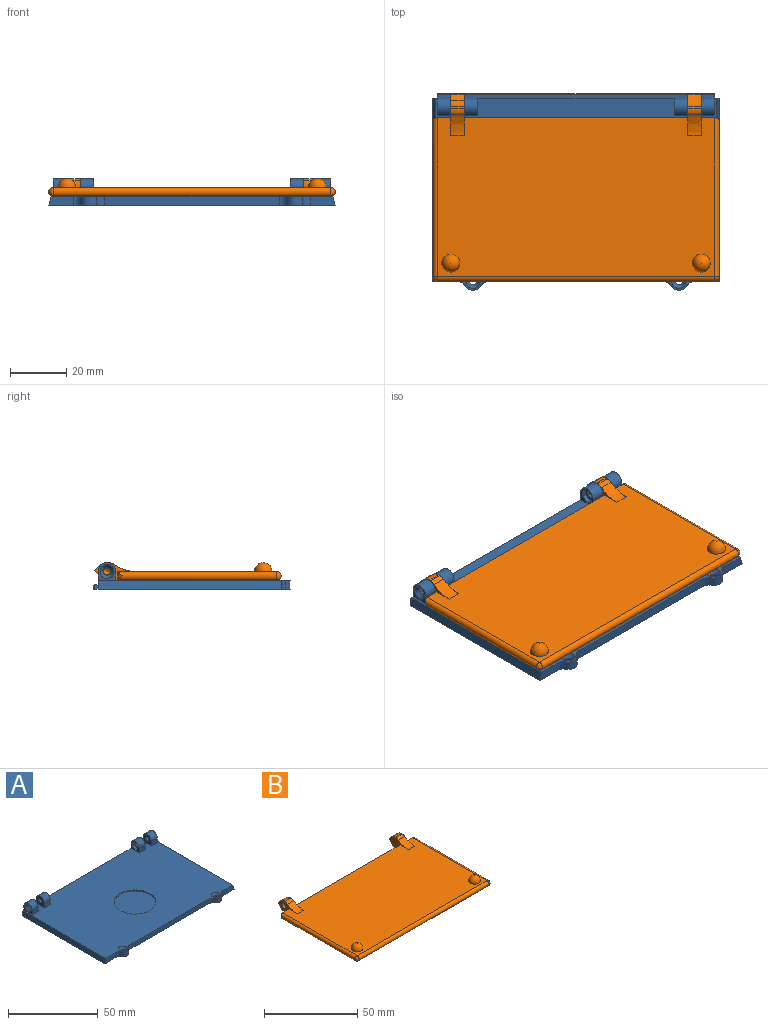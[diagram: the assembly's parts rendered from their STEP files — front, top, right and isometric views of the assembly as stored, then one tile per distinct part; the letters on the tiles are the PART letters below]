
ASSEMBLY  parts=2 mates=1
PART A: 66 faces, bbox 101.9x70.2x10.1 mm
  f0: plane 6.35x6.35mm, normal (-1,0,0), area 16.2mm2, adj f2,f9,f37,f39,f49,f50,f51,f52
  f1: plane 6.35x6.35mm, normal (1,0,0), area 16.2mm2, adj f2,f9,f32,f40,f42,f43,f44,f45
  f2: plane 100.27x68.62mm, normal (0,0,1), area 5950.8mm2, adj f0,f1,f3,f4,f8,f9,f12,f13
  f3: plane 8.77x3.18mm, normal (0,-1,0), area 26.6mm2, adj f2,f7,f15,f27,f65
  f4: plane 62x3.18mm, normal (0,-1,0), area 196.9mm2, adj f2,f7,f14,f16
  f5: plane 97.94x1.09mm, normal (0,1,0), area 107mm2, adj f22,f23,f24,f25
  f6: plane 98.45x1.32mm, normal (0,0,1), area 130mm2, adj f9,f10,f11,f24
  f7: plane 101.46x69.94mm, normal (0,0,-1), area 6733.1mm2, adj f3,f4,f8,f9,f10,f11,f12,f13
  f8: plane 8.77x3.18mm, normal (0,-1,0), area 26.6mm2, adj f2,f7,f17,f26,f64
  f9: plane 101.53x6.35mm, normal (0,1,0), area 222.8mm2, adj f0,f1,f2,f6,f7,f10,f11,f26
  f10: plane 1.6x1.32mm, normal (1,0,0), area 2.1mm2, adj f6,f7,f9,f25
  f11: plane 1.6x1.32mm, normal (-1,0,0), area 2.1mm2, adj f6,f7,f9,f22
  f12: cylinder r=3.17mm len=5.5mm, axis (0,0,1), area 21.1mm2, adj f2,f7,f14,f15
  f13: cylinder r=3.17mm len=5.5mm, axis (0,0,-1), area 21.1mm2, adj f2,f7,f16,f17
  f14: bspline ~3.49x2.75mm, area 10.6mm2, adj f2,f4,f7,f12
  f15: bspline ~3.49x2.75mm, area 10.6mm2, adj f2,f3,f7,f12
  f16: bspline ~3.49x2.75mm, area 10.6mm2, adj f2,f4,f7,f13
  f17: bspline ~3.49x2.75mm, area 10.6mm2, adj f2,f7,f8,f13
  f18: cylinder r=1.27mm len=2.54mm, axis (0,0,1), area 14.2mm2, adj f7,f20
  f19: cylinder r=1.27mm len=2.54mm, axis (0,0,1), area 14.2mm2, adj f7,f21
  f20: cone r=1.27mm half-angle=41deg, axis (0,0,1), area 21.8mm2, adj f2,f18
  f21: cone r=1.27mm half-angle=41deg, axis (0,0,1), area 21.8mm2, adj f2,f19
  f22: cylinder r=0.25mm len=1.6mm, axis (0,0,-1), area 0.5mm2, adj f5,f11,f23,f24
  f23: cylinder r=0.25mm len=98.45mm, axis (1,0,0), area 39.2mm2, adj f5,f7,f22,f25
  f24: cylinder r=0.25mm len=98.45mm, axis (-1,0,0), area 39.2mm2, adj f5,f6,f22,f25
  f25: cylinder r=0.25mm len=1.6mm, axis (0,0,1), area 0.5mm2, adj f5,f10,f23,f24
  f26: cylinder r=0.25mm len=65.08mm, axis (0,1,0), area 17.3mm2, adj f7,f8,f9,f64
  f27: cylinder r=0.25mm len=65.08mm, axis (0,-1,0), area 17.3mm2, adj f3,f7,f9,f65
  f28: plane 6.35x6.35mm, normal (-1,0,0), area 16.6mm2, adj f2,f9,f29,f41,f61
  f29: plane 4.76x3.18mm, normal (0,-1,0), area 15.1mm2, adj f2,f28,f30,f41
  f30: plane 6.35x6.35mm, normal (1,0,0), area 30.9mm2, adj f2,f9,f29,f41,f59
  f31: plane 6.35x6.35mm, normal (-1,0,0), area 30.9mm2, adj f2,f9,f32,f40,f57
  f32: plane 4.76x3.18mm, normal (0,-1,0), area 15.1mm2, adj f1,f2,f31,f40
  f33: plane 6.35x6.35mm, normal (1,0,0), area 16.6mm2, adj f2,f9,f35,f38,f60
  f34: plane 6.35x6.35mm, normal (-1,0,0), area 30.9mm2, adj f2,f9,f35,f38,f58
  f35: plane 4.76x3.18mm, normal (0,-1,0), area 15.1mm2, adj f2,f33,f34,f38
  f36: plane 6.35x6.35mm, normal (1,0,0), area 30.9mm2, adj f2,f9,f37,f39,f56
  f37: plane 4.76x3.18mm, normal (0,-1,0), area 15.1mm2, adj f0,f2,f36,f39
  f38: cylinder r=3.17mm len=6.35mm, axis (-1,0,0), area 47.5mm2, adj f9,f33,f34,f35
  f39: cylinder r=3.17mm len=6.35mm, axis (-1,0,0), area 47.5mm2, adj f0,f9,f36,f37
  f40: cylinder r=3.17mm len=6.35mm, axis (-1,0,0), area 47.5mm2, adj f1,f9,f31,f32
  f41: cylinder r=3.17mm len=6.35mm, axis (-1,0,0), area 47.5mm2, adj f9,f28,f29,f30
  f42: plane 2.39x1.6mm, normal (0,0.5,-0.87), area 4.4mm2, adj f1,f43,f47,f48
  f43: plane 2.76x1.6mm, normal (0,1,0), area 4.4mm2, adj f1,f42,f44,f48
  f44: plane 2.39x1.6mm, normal (0,0.5,0.87), area 4.4mm2, adj f1,f43,f45,f48
  f45: plane 2.39x1.6mm, normal (0,-0.5,0.87), area 4.4mm2, adj f1,f44,f46,f48
  f46: plane 2.76x1.6mm, normal (0,-1,0), area 4.4mm2, adj f1,f45,f47,f48
  f47: plane 2.39x1.6mm, normal (0,-0.5,-0.87), area 4.4mm2, adj f1,f42,f46,f48
  f48: plane 5.51x4.78mm, normal (1,0,0), area 14.7mm2, adj f42,f43,f44,f45,f46,f47,f57
  f49: plane 2.39x1.59mm, normal (0,-0.5,-0.87), area 4.4mm2, adj f0,f50,f54,f55
  f50: plane 2.76x1.59mm, normal (0,-1,0), area 4.4mm2, adj f0,f49,f51,f55
  f51: plane 2.39x1.59mm, normal (0,-0.5,0.87), area 4.4mm2, adj f0,f50,f52,f55
  f52: plane 2.39x1.59mm, normal (0,0.5,0.87), area 4.4mm2, adj f0,f51,f53,f55
  f53: plane 2.76x1.59mm, normal (0,1,0), area 4.4mm2, adj f0,f52,f54,f55
  f54: plane 2.39x1.59mm, normal (0,0.5,-0.87), area 4.4mm2, adj f0,f49,f53,f55
  f55: plane 5.51x4.78mm, normal (-1,0,0), area 14.7mm2, adj f49,f50,f51,f52,f53,f54,f56
  f56: cylinder r=1.27mm len=3.18mm, axis (-1,0,0), area 25.3mm2, adj f36,f55
  f57: cylinder r=1.27mm len=3.16mm, axis (1,0,0), area 25.2mm2, adj f31,f48
  f58: cylinder r=1.27mm len=3.37mm, axis (1,0,0), area 26.9mm2, adj f34,f60
  f59: cylinder r=1.27mm len=3.37mm, axis (-1,0,0), area 26.9mm2, adj f30,f61
  f60: cone r=1.27mm half-angle=41deg, axis (1,0,0), area 21.8mm2, adj f33,f58
  f61: cone r=1.27mm half-angle=41deg, axis (-1,0,0), area 21.8mm2, adj f28,f59
  f62: cylinder r=11.63mm len=23.26mm, axis (0,0,1), area 57.9mm2, adj f2,f63
  f63: plane 23.26x23.26mm, normal (0,0,1), area 425mm2, adj f62
  f64: plane 65.08x3.05mm, normal (-0.97,0,0.26), area 205.3mm2, adj f2,f8,f9,f26
  f65: plane 65.08x3.05mm, normal (0.97,0,0.26), area 205.3mm2, adj f2,f3,f9,f27
PART B: 36 faces, bbox 102.7x67.3x7.5 mm
  f0: cylinder r=3.17mm len=4.78mm, axis (-1,0,0), area 13.2mm2, adj f6,f9,f10,f22
  f1: cylinder r=3.17mm len=4.78mm, axis (-1,0,0), area 11.4mm2, adj f12,f13,f14,f19
  f2: plane 4.76x3.18mm, normal (0,1,0), area 15.1mm2, adj f5,f6,f13,f32
  f3: plane 79.35x3.18mm, normal (0,1,0), area 251.9mm2, adj f5,f6,f10,f12
  f4: plane 4.76x3.18mm, normal (0,1,0), area 15.1mm2, adj f5,f6,f9,f29
  f5: plane 98.43x56.36mm, normal (0,0,1), area 5422.8mm2, adj f2,f3,f4,f7,f8,f9,f10,f12
  f6: plane 98.43x60.18mm, normal (0,0,-1), area 5583.3mm2, adj f0,f2,f3,f4,f9,f10,f12,f13
  f7: sphere r=3.17mm, area 63.3mm2, adj f5
  f8: sphere r=3.17mm, area 63.3mm2, adj f5
  f9: plane 15.72x7.45mm, normal (1,0,0), area 37.5mm2, adj f0,f4,f5,f6,f11,f17,f18,f21
  f10: plane 15.72x7.45mm, normal (-1,0,0), area 43.8mm2, adj f0,f3,f5,f6,f11,f17,f18,f21
  f11: plane 4.78x0.65mm, normal (0,0,1), area 3.1mm2, adj f9,f10,f17,f18
  f12: plane 15.75x7.45mm, normal (1,0,0), area 43.9mm2, adj f1,f3,f5,f6,f14,f15,f16,f19
  f13: plane 15.75x7.45mm, normal (-1,0,0), area 37.6mm2, adj f1,f2,f5,f6,f14,f15,f16,f19
  f14: plane 4.78x0.65mm, normal (0,0,1), area 3.1mm2, adj f1,f12,f13,f16
  f15: cylinder r=3.17mm len=4.78mm, axis (-1,0,0), area 13.2mm2, adj f6,f12,f13,f20
  f16: cylinder r=3.17mm len=4.78mm, axis (1,0,0), area 9.8mm2, adj f12,f13,f14,f23
  f17: cylinder r=3.17mm len=4.78mm, axis (-1,0,0), area 13.1mm2, adj f9,f10,f11,f21
  f18: cylinder r=3.17mm len=4.78mm, axis (1,0,0), area 9.8mm2, adj f9,f10,f11,f24
  f19: plane 4.78x2.3mm, normal (0,0.64,0.77), area 14.3mm2, adj f1,f12,f13,f20
  f20: plane 4.78x2.43mm, normal (0,0.77,-0.64), area 15.1mm2, adj f12,f13,f15,f19
  f21: plane 4.78x2.03mm, normal (0,0.64,0.77), area 12.7mm2, adj f9,f10,f17,f22
  f22: plane 4.78x2.4mm, normal (0,0.77,-0.64), area 15mm2, adj f0,f9,f10,f21
  f23: bspline ~7.62x5.25mm, area 39.1mm2, adj f5,f12,f13,f16
  f24: bspline ~7.62x5.25mm, area 39.1mm2, adj f5,f9,f10,f18
  f25: cone r=0mm half-angle=59deg, axis (-1,0,0), area 7.4mm2, adj f26
  f26: cylinder r=1.42mm len=3.18mm, axis (-1,0,0), area 28.4mm2, adj f13,f25
  f27: cone r=0mm half-angle=59deg, axis (1,0,0), area 7.4mm2, adj f28
  f28: cylinder r=1.42mm len=3.18mm, axis (1,0,0), area 28.4mm2, adj f9,f27
  f29: cylinder r=1.59mm len=3.18mm, axis (0,0,1), area 4mm2, adj f4,f30
  f30: cylinder r=1.59mm len=56.36mm, axis (0,-1,0), area 277.1mm2, adj f5,f6,f29,f31
  f31: sphere r=1.59mm, area 7.9mm2, adj f30,f33
  f32: cylinder r=1.59mm len=3.18mm, axis (0,0,-1), area 4mm2, adj f2,f34
  f33: cylinder r=1.59mm len=98.43mm, axis (-1,0,0), area 490.9mm2, adj f5,f6,f31,f35
  f34: cylinder r=1.59mm len=56.36mm, axis (0,1,0), area 277.1mm2, adj f5,f6,f32,f35
  f35: sphere r=1.59mm, area 7.9mm2, adj f33,f34
PLACE A t=(0,2.53,-3.45)mm fixed
PLACE B rot(axis=(-1,0,0),0deg) t=(0,0.61,-0.27)mm
MATE revolute B.f0 <-> A.f39  axis (1,0,0) through (44.45,31.02,2.9)mm
